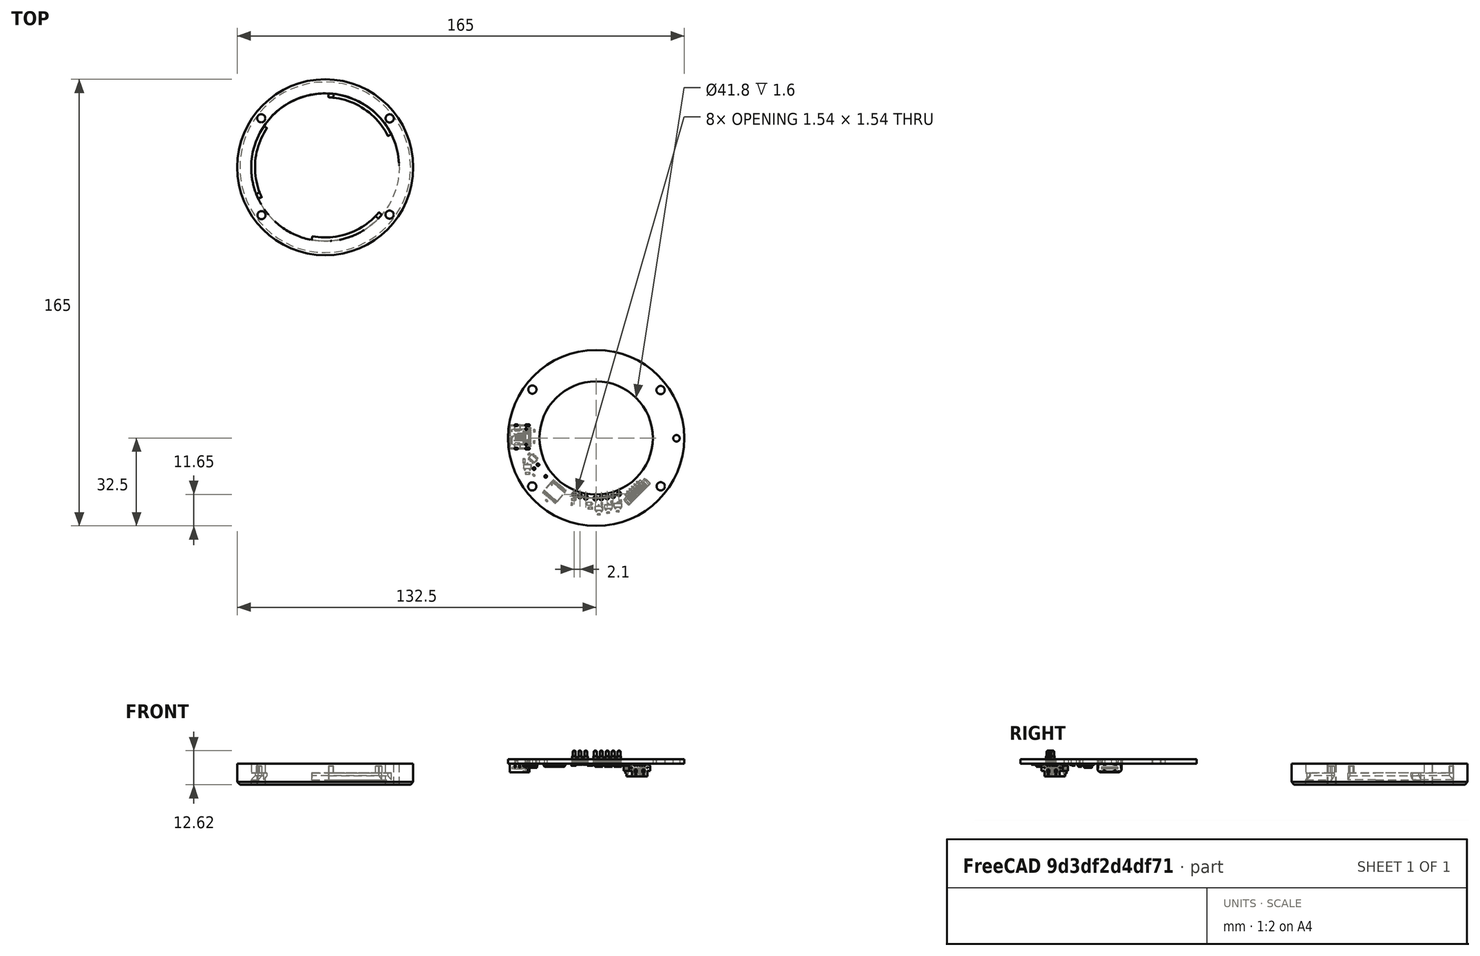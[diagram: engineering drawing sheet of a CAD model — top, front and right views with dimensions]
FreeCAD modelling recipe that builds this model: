
FCSTD DOCUMENT  (FreeCAD 0.18.4R)
Label: lensmount_3d
License: All rights reserved
LicenseURL: http://en.wikipedia.org/wiki/All_rights_reserved
objects: Part::Feature×35, Part::Cylinder×6, Part::Cut×6, App::Part×5, Part::MultiFuse×1, Part::Chamfer×1, Part::Box×1, PartDesign::CoordinateSystem×1, Sketcher::SketchObject×1
note: 52 computed .brp shape members not serialized (recipe doc carries the construction recipe); baked Part::Feature solids carry a one-line shape summary decoded from their .brp

FEATURE [Part::Feature] Part__Feature  label="Document"
  Placement = pos=(101.191,-50.7435,-23.243) rot=(0,0,1;0rad)
  shape: bbox 75.75 x 78.49 x 45.6 mm, 93 faces (baked)
FEATURE [Part::Cylinder] Cylinder
  Angle = 360
  AttacherType = Attacher::AttachEngine3D
  Height = 38.4
  Placement = pos=(0,0,-40) rot=(0,0,1;0rad)
  Radius = 32.5
FEATURE [Part::Cylinder] Cylinder001
  Angle = 360
  AttacherType = Attacher::AttachEngine3D
  Height = 45
  Placement = pos=(0,0,-42) rot=(0,0,1;0rad)
  Radius = 29
FEATURE [Part::Cut] Cut
  Base = -> Cylinder
  Tool = -> Cylinder001
FEATURE [Part::MultiFuse] Fusion
  Shapes = -> [Part__Feature,Cut]
FEATURE [Part::Chamfer] Chamfer
  Base = -> Fusion
  Edges = 1 edges r=1: [Edge193]
  Placement = pos=(0,0,0) rot=(0,0,1;0.05236rad)
FEATURE [Part::Cylinder] Cylinder002
  Angle = 360
  AttacherType = Attacher::AttachEngine3D
  Height = 50
  Placement = pos=(23.77,-17.5,-45) rot=(0,0,1;0rad)
  Radius = 1.5
FEATURE [Part::Cylinder] Cylinder003
  Angle = 360
  AttacherType = Attacher::AttachEngine3D
  Height = 50
  Placement = pos=(-23.52,-17.68,-45) rot=(0,0,1;0rad)
  Radius = 1.5
FEATURE [Part::Cylinder] Cylinder004
  Angle = 360
  AttacherType = Attacher::AttachEngine3D
  Height = 50
  Placement = pos=(23.8,18.05,-45) rot=(0,0,1;0rad)
  Radius = 1.5
FEATURE [Part::Cylinder] Cylinder005
  Angle = 360
  AttacherType = Attacher::AttachEngine3D
  Height = 50
  Placement = pos=(-23.6,18.08,-45) rot=(0,0,1;0rad)
  Radius = 1.5
FEATURE [Part::Cut] Cut001
  Base = -> Chamfer
  Tool = -> Cylinder002
FEATURE [Part::Cut] Cut002
  Base = -> Cut001
  Tool = -> Cylinder004
FEATURE [Part::Cut] Cut003
  Base = -> Cut002
  Tool = -> Cylinder005
FEATURE [Part::Cut] Cut004
  Base = -> Cut003
  Placement = pos=(0,0,30.61) rot=(0,0,1;0rad)
  Tool = -> Cylinder003
FEATURE [Part::Box] Box  label="Cube"
  AttacherType = Attacher::AttachEngine3D
  Height = 40
  Length = 100
  Placement = pos=(-50,-50,-1.6) rot=(0,0,1;0rad)
  Width = 100
FEATURE [Part::Cut] Cut005
  Base = -> Cut004
  Tool = -> Box
FEATURE [Part::Feature] Shape032  label="R6_R_0402_1005Metric_5F3EFFFB001"
  Placement = pos=(105.7,-123.7,-1.6) rot=(0.707107,0.707107,0;3.14159rad)
  shape: bbox 0.5 x 1 x 0.35 mm, 26 faces (baked)
FEATURE [Part::Feature] Shape033  label="R7_R_0402_1005Metric_5F3F0E057"
  Placement = pos=(102.2,-124.3,-1.6) rot=(0.707107,0.707107,0;3.14159rad)
  shape: bbox 0.5 x 1 x 0.35 mm, 26 faces (baked)
FEATURE [Part::Feature] Shape034  label="U2_SOT_23_5F3F006B001"
  Placement = pos=(74.6464,-110.571,-1.6) rot=(0.707107,0.707107,0;3.14159rad)
  shape: bbox 3 x 2.5 x 1.2 mm, 76 faces (baked)
FEATURE [Part::Feature] Shape035  label="R9_R_0402_1005Metric_5F3F0011"
  Placement = pos=(91,-124.4,-1.6) rot=(0.707107,-0.707107,0;3.14159rad)
  shape: bbox 0.5 x 1 x 0.35 mm, 26 faces (baked)
FEATURE [Part::Feature] Shape036  label="U3_SOT_23_6_5F3F1C038"
  Placement = pos=(76.7,-107.6,-1.6) rot=(-0.382683,0.92388,0;3.14159rad)
  shape: bbox 3.677 x 3.677 x 1.55 mm, 124 faces (baked)
FEATURE [PartDesign::CoordinateSystem] Local_CS_cc020
  AttacherType = Attacher::AttachEngine3D
FEATURE [Part::Feature] Pcb_cc020
  shape: bbox 65 x 65 x 1.6 mm, 46 faces (baked)
FEATURE [Sketcher::SketchObject] PCB_Sketch_cc020
  sketch-geometry (7):
    g0: Circle CenterX=129.65 CenterY=-100.125 CenterZ=0 NormalX=0 NormalY=0 NormalZ=1 AngleXU=0 Radius=1.20104
    g1: Circle CenterX=123.825 CenterY=-117.85 CenterZ=0 NormalX=0 NormalY=0 NormalZ=1 AngleXU=0 Radius=1.52316
    g2: Circle CenterX=123.775 CenterY=-82.3 CenterZ=0 NormalX=0 NormalY=0 NormalZ=1 AngleXU=0 Radius=1.52315
    g3: Circle CenterX=76.475 CenterY=-82.125 CenterZ=0 NormalX=0 NormalY=0 NormalZ=1 AngleXU=0 Radius=1.52316
    g4: Circle CenterX=76.4 CenterY=-117.9 CenterZ=0 NormalX=0 NormalY=0 NormalZ=1 AngleXU=0 Radius=1.52315
    g5: Circle CenterX=100 CenterY=-100 CenterZ=0 NormalX=0 NormalY=0 NormalZ=1 AngleXU=0 Radius=20.9
    g6: Circle CenterX=100 CenterY=-100 CenterZ=0 NormalX=0 NormalY=0 NormalZ=1 AngleXU=0 Radius=32.5
FEATURE [App::Part] Board_Geoms_cc020  label="Board_Geoms_cc022"
  Group = -> [Local_CS_cc020,Pcb_cc020,PCB_Sketch_cc020]
  Origin = -> Origin007
FEATURE [Part::Feature] Shape037  label="R5_R_0402_1005Metric_5F3EFFF005"
  Placement = pos=(108,-127.1,-1.6) rot=(0,1,0;3.14159rad)
  shape: bbox 1 x 0.5 x 0.35 mm, 26 faces (baked)
FEATURE [Part::Feature] Shape038  label="R4_R_0402_1005Metric_5F3EFFED001"
  Placement = pos=(101,-128.2,-1.6) rot=(0,1,0;3.14159rad)
  shape: bbox 1 x 0.5 x 0.35 mm, 26 faces (baked)
FEATURE [Part::Feature] Shape039  label="R3_R_0402_1005Metric_5F3EFFE007"
  Placement = pos=(104.5,-127.6,-1.6) rot=(0,1,0;3.14159rad)
  shape: bbox 1 x 0.5 x 0.35 mm, 26 faces (baked)
FEATURE [Part::Feature] Shape040  label="R2_R_0402_1005Metric_5F3EFFDF001"
  Placement = pos=(77.2,-97.4,-1.6) rot=(0.707107,-0.707107,0;3.14159rad)
  shape: bbox 0.5 x 1 x 0.35 mm, 26 faces (baked)
FEATURE [Part::Feature] Shape041  label="R1_R_0402_1005Metric_5F3EFFD009"
  Placement = pos=(77.2,-101.5,-1.6) rot=(0.707107,0.707107,0;3.14159rad)
  shape: bbox 0.5 x 1 x 0.35 mm, 26 faces (baked)
FEATURE [Part::Feature] Shape042  label="Q3_SOT_23_5F3EFFD002"
  Placement = pos=(108,-124.9,-1.6) rot=(0.707107,0.707107,0;3.14159rad)
  shape: bbox 3 x 2.5 x 1.2 mm, 76 faces (baked)
FEATURE [Part::Feature] Shape043  label="Q2_SOT_23_5F3F0DD004"
  Placement = pos=(101,-126,-1.6) rot=(0.707107,0.707107,0;3.14159rad)
  shape: bbox 3 x 2.5 x 1.2 mm, 76 faces (baked)
FEATURE [Part::Feature] Shape044  label="Q1_SOT_23_5F3EFFA008"
  Placement = pos=(104.5,-125.4,-1.6) rot=(0.707107,0.707107,0;3.14159rad)
  shape: bbox 3 x 2.5 x 1.2 mm, 76 faces (baked)
FEATURE [Part::Feature] Shape045  label="C6_C_0603_1608Metric_5F3EFEC003"
  Placement = pos=(91.7,-122.7,-1.6) rot=(1,0,0;3.14159rad)
  shape: bbox 1.6 x 0.8 x 0.8 mm, 28 faces (baked)
FEATURE [Part::Feature] Shape046  label="J10_Molex_53398_0571_5F3EFF7D001"
  Placement = pos=(114.2,-119,-1.6) rot=(-0.382683,0.92388,0;3.14159rad)
  shape: bbox 9.758 x 9.758 x 4.7 mm, 201 faces (baked)
FEATURE [Part::Feature] Shape047  label="C7_C_0603_1608Metric_5F3EFEC010"
  Placement = pos=(97.9,-126,-1.6) rot=(0,1,0;3.14159rad)
  shape: bbox 1.6 x 0.8 x 0.8 mm, 28 faces (baked)
FEATURE [Part::Feature] Shape048  label="C3_C_0603_1608Metric_5F3EFEAD001"
  Placement = pos=(73.3,-108.5,-1.6) rot=(0.707107,-0.707107,0;3.14159rad)
  shape: bbox 0.8 x 1.6 x 0.8 mm, 28 faces (baked)
FEATURE [Part::Feature] Shape049  label="C4_C_0603_1608Metric_5F3EFEB005"
  Placement = pos=(74.6464,-112.975,-1.6) rot=(1,0,0;3.14159rad)
  shape: bbox 1.6 x 0.8 x 0.8 mm, 28 faces (baked)
FEATURE [Part::Feature] Shape050  label="D1_D_SOD_323F_5F3EFEE002"
  Placement = pos=(97.5,-124.3,-1.6) rot=(0,1,0;3.14159rad)
  shape: bbox 2.5 x 1.25 x 0.73 mm, 27 faces (baked)
FEATURE [Part::Feature] Shape051  label="C5_C_0402_1005Metric_5F3EFEBB001"
  Placement = pos=(75.2,-105.9,-1.6) rot=(0.92388,0.382683,0;3.14159rad)
  shape: bbox 1.061 x 1.061 x 0.5 mm, 28 faces (baked)
FEATURE [Part::Feature] Shape052  label="C1_C_0402_1005Metric_5F3EFE9F001"
  Placement = pos=(81.7,-123.2,-1.6) rot=(0.92388,-0.382683,0;3.14159rad)
  shape: bbox 1.061 x 1.061 x 0.5 mm, 28 faces (baked)
FEATURE [Part::Feature] Shape053  label="C2_C_0402_1005Metric_5F3EFEA007"
  Placement = pos=(77,-113.75,-1.6) rot=(0.382683,0.92388,0;3.14159rad)
  shape: bbox 1.061 x 1.061 x 0.5 mm, 28 faces (baked)
FEATURE [Part::Feature] Shape054  label="J9_HRO_TYPE-C-31-M-12(1)_5F3EFB50"
  Placement = pos=(68.1,-104.1,-1.6) rot=(0.707107,0.707107,0;3.14159rad)
  shape: bbox 7.9 x 8.95 x 4.2 mm, 570 faces, 4 solids (baked)
FEATURE [Part::Feature] Shape055  label="U1_TSSOP_20_44x65mm_P065mm_5F3EF99D001"
  Placement = pos=(84.6,-119.8,-1.6) rot=(-0.422618,0.906308,0;3.14159rad)
  shape: bbox 8.794 x 8.83 x 1.2 mm, 336 faces (baked)
FEATURE [Part::Feature] Shape056  label="J7_mill-max-0964-0-15-20-85-14-11-0_5F3EEFB006"
  Placement = pos=(106.275,-121.4,-2) rot=(0,-1,0;1.5708rad)
  shape: bbox 1.829 x 1.829 x 5.232 mm, 19 faces (baked)
FEATURE [Part::Feature] Shape057  label="J1_mill-max-0964-0-15-20-85-14-11-0_5F3EEFA002"
  Placement = pos=(91.9,-120.85,-2) rot=(0,-1,0;1.5708rad)
  shape: bbox 1.829 x 1.829 x 5.232 mm, 19 faces (baked)
FEATURE [Part::Feature] Shape058  label="J4_mill-max-0964-0-15-20-85-14-11-0_5F3EEFBA001"
  Placement = pos=(99.7,-122.325,-2) rot=(0,-1,0;1.5708rad)
  shape: bbox 1.829 x 1.829 x 5.232 mm, 19 faces (baked)
FEATURE [Part::Feature] Shape059  label="J5_mill-max-0964-0-15-20-85-14-11-0_5F3EEFC005"
  Placement = pos=(101.9,-122.2,-2) rot=(0,-1,0;1.5708rad)
  shape: bbox 1.829 x 1.829 x 5.232 mm, 19 faces (baked)
FEATURE [Part::Feature] Shape060  label="J3_mill-max-0964-0-15-20-85-14-11-0_5F3EEFB001"
  Placement = pos=(96.175,-122,-2) rot=(0,-1,0;1.5708rad)
  shape: bbox 1.829 x 1.829 x 5.232 mm, 19 faces (baked)
FEATURE [Part::Feature] Shape061  label="J2_mill-max-0964-0-15-20-85-14-11-0_5F3EEFA007"
  Placement = pos=(94,-121.5,-2) rot=(0,-1,0;1.5708rad)
  shape: bbox 1.829 x 1.829 x 5.232 mm, 19 faces (baked)
FEATURE [Part::Feature] Shape062  label="J6_mill-max-0964-0-15-20-85-14-11-0_5F3EEFBF001"
  Placement = pos=(104.125,-121.875,-2) rot=(0,-1,0;1.5708rad)
  shape: bbox 1.829 x 1.829 x 5.232 mm, 19 faces (baked)
FEATURE [Part::Feature] Shape063  label="J8_mill-max-0964-0-15-20-85-14-11-0_5F3EEFAB001"
  Placement = pos=(108.425,-120.65,-2) rot=(0,-1,0;1.5708rad)
  shape: bbox 1.829 x 1.829 x 5.232 mm, 19 faces (baked)
FEATURE [App::Part] Top_cc020  label="Top_cc021"
  Group = -> [Shape059,Shape062,Shape058,Shape056,Shape060,Shape063,Shape061,Shape057]
  Origin = -> Origin005
FEATURE [Part::Feature] Shape064  label="R8_R_0402_1005Metric_5F3F0010"
  Placement = pos=(109.2,-123.3,-1.6) rot=(0.707107,0.707107,0;3.14159rad)
  shape: bbox 0.5 x 1 x 0.35 mm, 26 faces (baked)
FEATURE [App::Part] Bot_cc020  label="Bot_cc021"
  Group = -> [Shape036,Shape034,Shape035,Shape064,Shape033,Shape032,Shape037,Shape038,Shape039,Shape040,Shape041,Shape042,Shape043,Shape044,Shape046,Shape050,Shape047,Shape045,Shape051,Shape049,Shape048,Shape053,Shape052,Shape054,Shape055]
  Origin = -> Origin009
FEATURE [App::Part] Step_Models_cc020  label="Step_Models_cc021"
  Group = -> [Top_cc020,Bot_cc020]
  Origin = -> Origin006
FEATURE [App::Part] Board_cc020  label="lensmount-v1"
  Group = -> [Board_Geoms_cc020,Step_Models_cc020]
  Origin = -> Origin008
  Placement = pos=(-100,-99.82,-1.6) rot=(1,0,0;3.14159rad)
